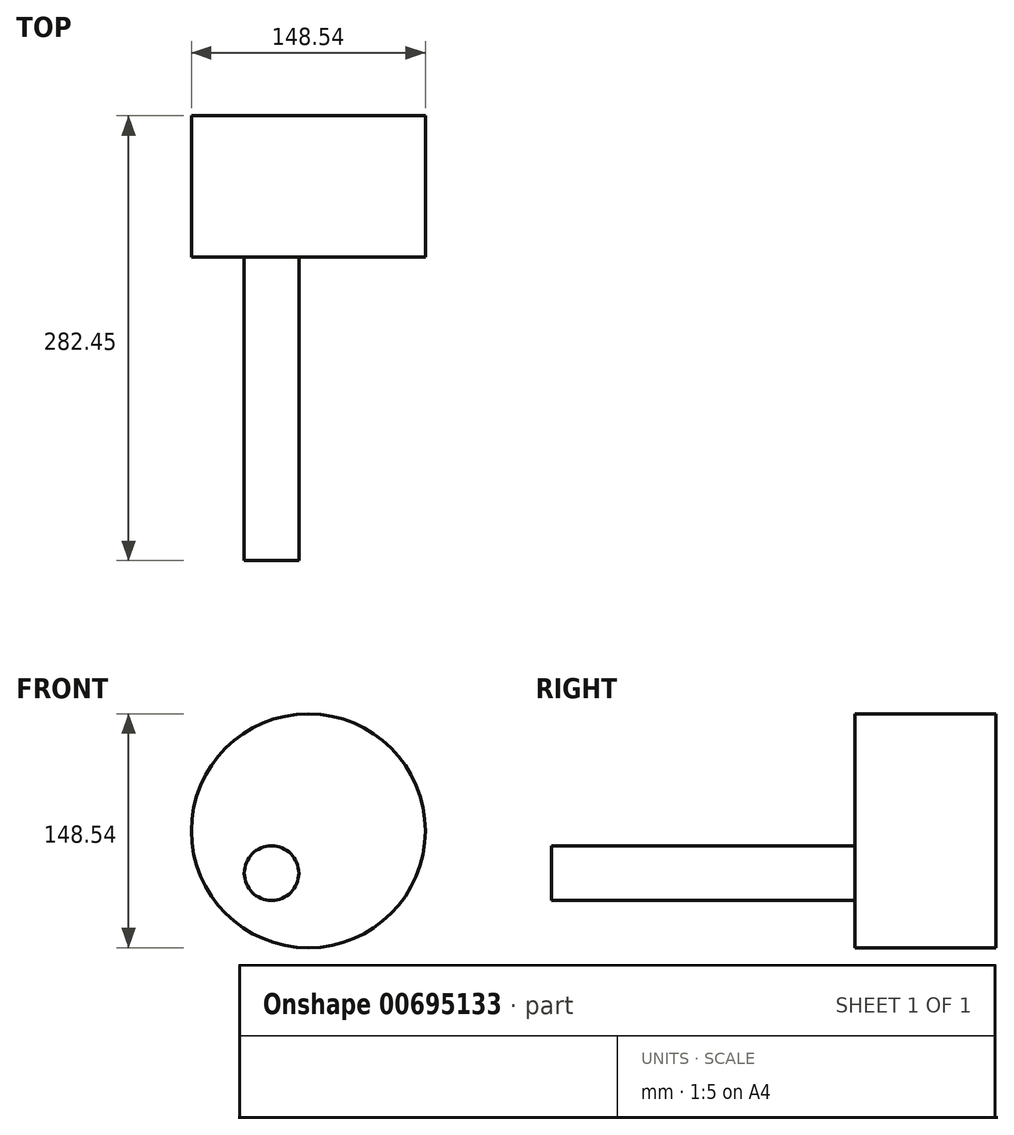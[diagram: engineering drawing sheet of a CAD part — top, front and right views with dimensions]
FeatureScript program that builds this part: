
annotation { "Feature Type Name" : "Feature", "Feature Type Description" : "" }
export const myFeature = defineFeature(function(context is Context, id is Id, definition is map)
    precondition{}
    {
        {
            var Q0;
            Q0=qCreatedBy(makeId("Front.planeOp"),FACE);
            var sketch = newSketch(context, id + "F0", { "sketchPlane" : qUnion([Q0])});
            skCircle(sketch, "E0", {"center": v(-35.81, 37.41) * mm, "radius": 17.31 * mm});
            skSolve(sketch);
        }
        {
            var Q0;
            Q0=makeQuery(id+"F0.imprint","IMPRINT",FACE,{"disambiguationData":[TD([[makeQuery(id+"F0.imprint","IMPRINT",EDGE,{"derivedFrom":sQuery(id+"F0.wireOp",EDGE,"E0")}),1.0]])]});
            extrude(context, id + "F1", {"entities" : qUnion([Q0]), "depth" : 192.79 * mm, "offsetDistance" : 25.4 * mm});
        }
        {
            var Q0;
            Q0=qCreatedBy(makeId("Front.planeOp"),FACE);
            var sketch = newSketch(context, id + "F2", { "sketchPlane" : qUnion([Q0])});
            skCircle(sketch, "E1", {"center": v(-12.4, 64.28) * mm, "radius": 74.27 * mm});
            skSolve(sketch);
        }
        {
            var Q0;
            Q0=makeQuery(id+"F2.imprint","IMPRINT",FACE,{"disambiguationData":[TD([[makeQuery(id+"F2.imprint","IMPRINT",EDGE,{"derivedFrom":sQuery(id+"F2.wireOp",EDGE,"E1")}),1.0]])]});
            extrude(context, id + "F3", {"entities" : qUnion([Q0]), "operationType" : NewBodyOperationType.ADD, "oppositeDirection" : true, "depth" : 89.66 * mm, "offsetDistance" : 25.4 * mm});
        }
    });
